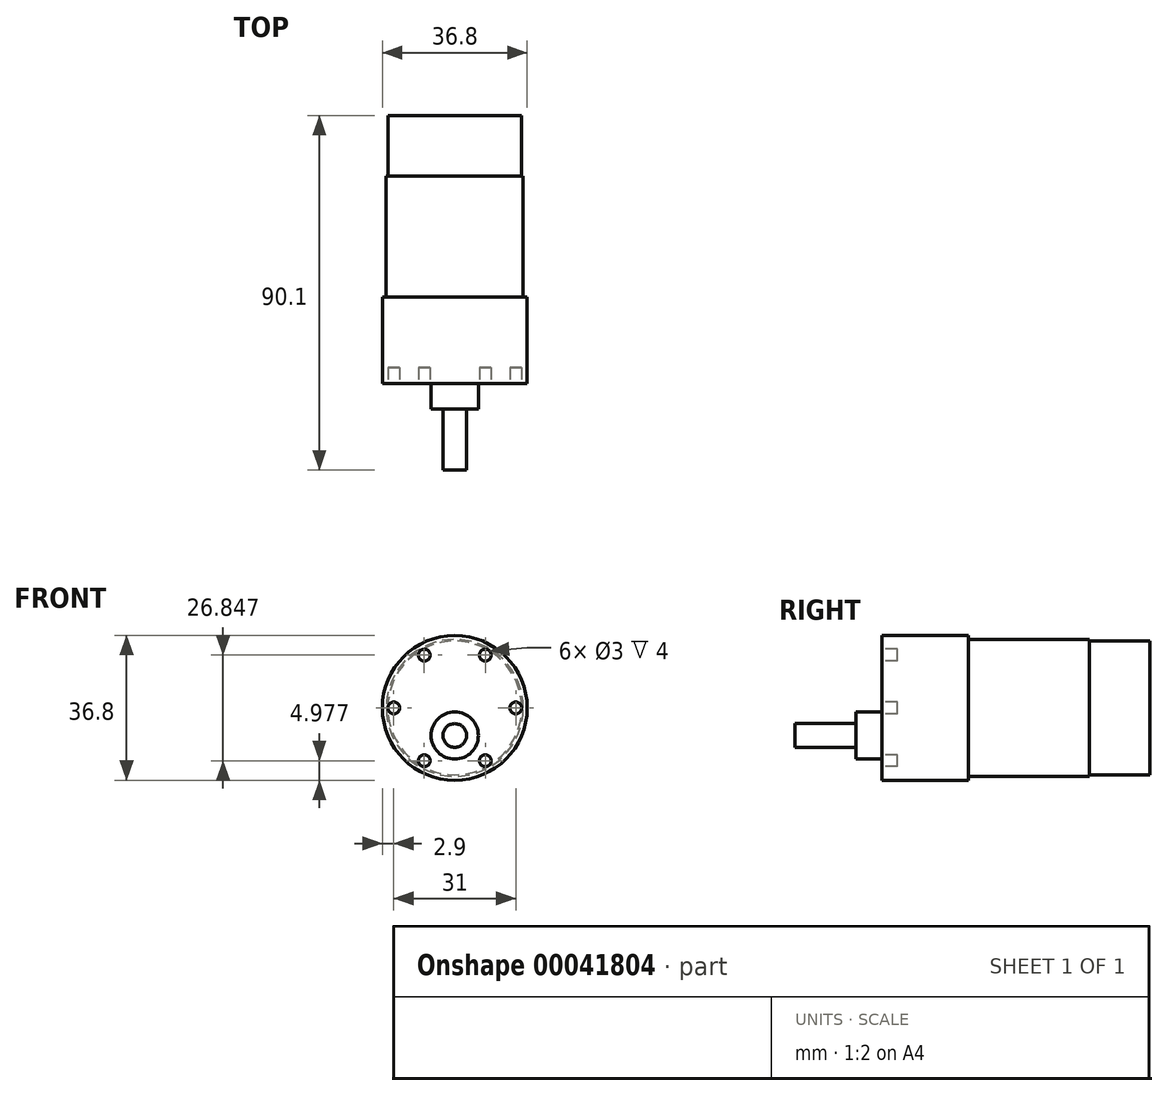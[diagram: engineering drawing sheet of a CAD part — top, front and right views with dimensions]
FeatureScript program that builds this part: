
annotation { "Feature Type Name" : "Feature", "Feature Type Description" : "" }
export const myFeature = defineFeature(function(context is Context, id is Id, definition is map)
    precondition{}
    {
        {
            var Q0;
            Q0=qCreatedBy(makeId("Front.planeOp"),FACE);
            var sketch = newSketch(context, id + "F0", { "sketchPlane" : qUnion([Q0])});
            skCircle(sketch, "E0", {"center": v(0, 0) * mm, "radius": 18.4 * mm});
            skSolve(sketch);
        }
        {
            var Q0;
            Q0=makeQuery(id+"F0.imprint","IMPRINT",FACE,{"disambiguationData":[TD([[makeQuery(id+"F0.imprint","IMPRINT",EDGE,{"derivedFrom":sQuery(id+"F0.wireOp",EDGE,"E0")}),1.0]])]});
            extrude(context, id + "F1", {"entities" : qUnion([Q0]), "oppositeDirection" : true, "depth" : 22 * mm});
        }
        {
            var Q0;
            Q0=makeQuery(id+"F1.opExtrude","CAP_FACE",FACE,{"disambiguationData":[OSD([sQuery(id+"F0.wireOp",EDGE,"E0")])],"isStart":false});
            var sketch = newSketch(context, id + "F2", { "sketchPlane" : qUnion([Q0])});
            skCircle(sketch, "E1", {"center": v(0, 0) * mm, "radius": 17.4 * mm});
            skSolve(sketch);
        }
        {
            var Q0;
            Q0=makeQuery(id+"F2.imprint","IMPRINT",FACE,{"disambiguationData":[TD([[makeQuery(id+"F2.imprint","IMPRINT",EDGE,{"derivedFrom":sQuery(id+"F2.wireOp",EDGE,"E1")}),1.0]])]});
            extrude(context, id + "F3", {"entities" : qUnion([Q0]), "operationType" : NewBodyOperationType.ADD, "depth" : 30.7 * mm});
        }
        {
            var Q0;
            Q0=makeQuery(id+"F3.opExtrude","CAP_FACE",FACE,{"disambiguationData":[OSD([sQuery(id+"F2.wireOp",EDGE,"E1")])],"isStart":false});
            var sketch = newSketch(context, id + "F4", { "sketchPlane" : qUnion([Q0])});
            skCircle(sketch, "E2", {"center": v(0, 0) * mm, "radius": 17 * mm});
            skSolve(sketch);
        }
        {
            var Q0;
            Q0=makeQuery(id+"F4.imprint","IMPRINT",FACE,{"disambiguationData":[TD([[makeQuery(id+"F4.imprint","IMPRINT",EDGE,{"derivedFrom":sQuery(id+"F4.wireOp",EDGE,"E2")}),1.0]])]});
            extrude(context, id + "F5", {"entities" : qUnion([Q0]), "operationType" : NewBodyOperationType.ADD, "depth" : 15.4 * mm});
        }
        {
            var Q0;
            Q0=makeQuery(id+"F1.opExtrude","CAP_FACE",FACE,{"disambiguationData":[OSD([sQuery(id+"F0.wireOp",EDGE,"E0")])],"isStart":true});
            var sketch = newSketch(context, id + "F6", { "sketchPlane" : qUnion([Q0])});
            skCircle(sketch, "E3", {"center": v(0, -7) * mm, "radius": 6 * mm});
            skSolve(sketch);
        }
        {
            var Q0;
            Q0=makeQuery(id+"F6.imprint","IMPRINT",FACE,{"disambiguationData":[TD([[makeQuery(id+"F6.imprint","IMPRINT",EDGE,{"derivedFrom":sQuery(id+"F6.wireOp",EDGE,"E3")}),1.0]])]});
            extrude(context, id + "F7", {"entities" : qUnion([Q0]), "operationType" : NewBodyOperationType.ADD, "depth" : 6.5 * mm});
        }
        {
            var Q0;
            Q0=makeQuery(id+"F7.opExtrude","CAP_FACE",FACE,{"disambiguationData":[OSD([sQuery(id+"F6.wireOp",EDGE,"E3")])],"isStart":false});
            var sketch = newSketch(context, id + "F8", { "sketchPlane" : qUnion([Q0])});
            skCircle(sketch, "E4", {"center": v(0, -7) * mm, "radius": 3 * mm});
            skSolve(sketch);
        }
        {
            var Q0;
            Q0=makeQuery(id+"F8.imprint","IMPRINT",FACE,{"disambiguationData":[TD([[makeQuery(id+"F8.imprint","IMPRINT",EDGE,{"derivedFrom":sQuery(id+"F8.wireOp",EDGE,"E4")}),1.0]])]});
            extrude(context, id + "F9", {"entities" : qUnion([Q0]), "operationType" : NewBodyOperationType.ADD, "depth" : (22 - 6.5) * mm});
        }
        {
            var Q0;
            Q0=makeQuery(id+"F1.opExtrude","CAP_FACE",FACE,{"disambiguationData":[OSD([sQuery(id+"F0.wireOp",EDGE,"E0")])],"isStart":true});
            var sketch = newSketch(context, id + "F10", { "sketchPlane" : qUnion([Q0])});
            skCircle(sketch, "E5", {"center": v(0, 0) * mm, "radius": 15.5 * mm, "construction": true});
            skCircle(sketch, "E6", {"center": v(-15.5, 0) * mm, "radius": 1.5 * mm});
            skCircle(sketch, "E7", {"center": v(15.5, 0) * mm, "radius": 1.5 * mm});
            skCircle(sketch, "E8", {"center": v(7.75, -13.42) * mm, "radius": 1.5 * mm});
            skCircle(sketch, "E9", {"center": v(-7.75, -13.42) * mm, "radius": 1.5 * mm});
            skCircle(sketch, "E10", {"center": v(-7.75, 13.42) * mm, "radius": 1.5 * mm});
            skCircle(sketch, "E11", {"center": v(7.75, 13.42) * mm, "radius": 1.5 * mm});
            skSolve(sketch);
        }
        {
            var Q0;
            Q0=makeQuery(id+"F10.imprint","IMPRINT",FACE,{"disambiguationData":[TD([[makeQuery(id+"F10.imprint","IMPRINT",EDGE,{"derivedFrom":sQuery(id+"F10.wireOp",EDGE,"E6")}),1.0]])]});
            var Q1;
            Q1=makeQuery(id+"F10.imprint","IMPRINT",FACE,{"disambiguationData":[TD([[makeQuery(id+"F10.imprint","IMPRINT",EDGE,{"derivedFrom":sQuery(id+"F10.wireOp",EDGE,"E10")}),1.0]])]});
            var Q2;
            Q2=makeQuery(id+"F10.imprint","IMPRINT",FACE,{"disambiguationData":[TD([[makeQuery(id+"F10.imprint","IMPRINT",EDGE,{"derivedFrom":sQuery(id+"F10.wireOp",EDGE,"E11")}),1.0]])]});
            var Q3;
            Q3=makeQuery(id+"F10.imprint","IMPRINT",FACE,{"disambiguationData":[TD([[makeQuery(id+"F10.imprint","IMPRINT",EDGE,{"derivedFrom":sQuery(id+"F10.wireOp",EDGE,"E7")}),1.0]])]});
            var Q4;
            Q4=makeQuery(id+"F10.imprint","IMPRINT",FACE,{"disambiguationData":[TD([[makeQuery(id+"F10.imprint","IMPRINT",EDGE,{"derivedFrom":sQuery(id+"F10.wireOp",EDGE,"E9")}),1.0]])]});
            var Q5;
            Q5=makeQuery(id+"F10.imprint","IMPRINT",FACE,{"disambiguationData":[TD([[makeQuery(id+"F10.imprint","IMPRINT",EDGE,{"derivedFrom":sQuery(id+"F10.wireOp",EDGE,"E8")}),1.0]])]});
            extrude(context, id + "F11", {"entities" : qUnion([Q0, Q1, Q2, Q3, Q4, Q5]), "operationType" : NewBodyOperationType.REMOVE, "oppositeDirection" : true, "depth" : 4 * mm});
        }
    });
